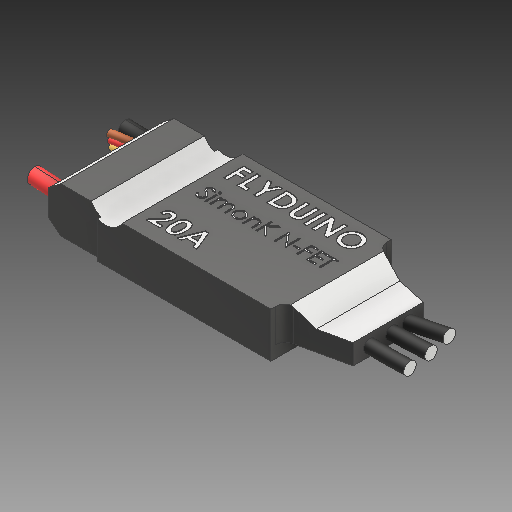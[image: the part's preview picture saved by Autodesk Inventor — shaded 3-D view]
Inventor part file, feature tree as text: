
AUTODESK INVENTOR PART (.ipt)
format: ipt  version: 2018 (Build 220112000, 112)  size: 1,011,712 bytes
history: native  units: mm
features: other x3, sketch x1
ambient origin geometry x8: Origin, YZ Plane, XZ Plane, XY Plane, X Axis, Y Axis, Z Axis, Center Point
bodies: Volumenkörper1 (feature_tree)
feature tree (4):
  other  "28-2-2013-001 - ESC Flyduino SimonK 20A body_MIR.ipt"
  other  "Volumenkörper1::28-2-2013-001 - ESC Flyduino SimonK 20A body_MIR.ipt"
  other  "Bezeichnung1"
  sketch  "Skizze1"  dims[d0=10.0mm]
